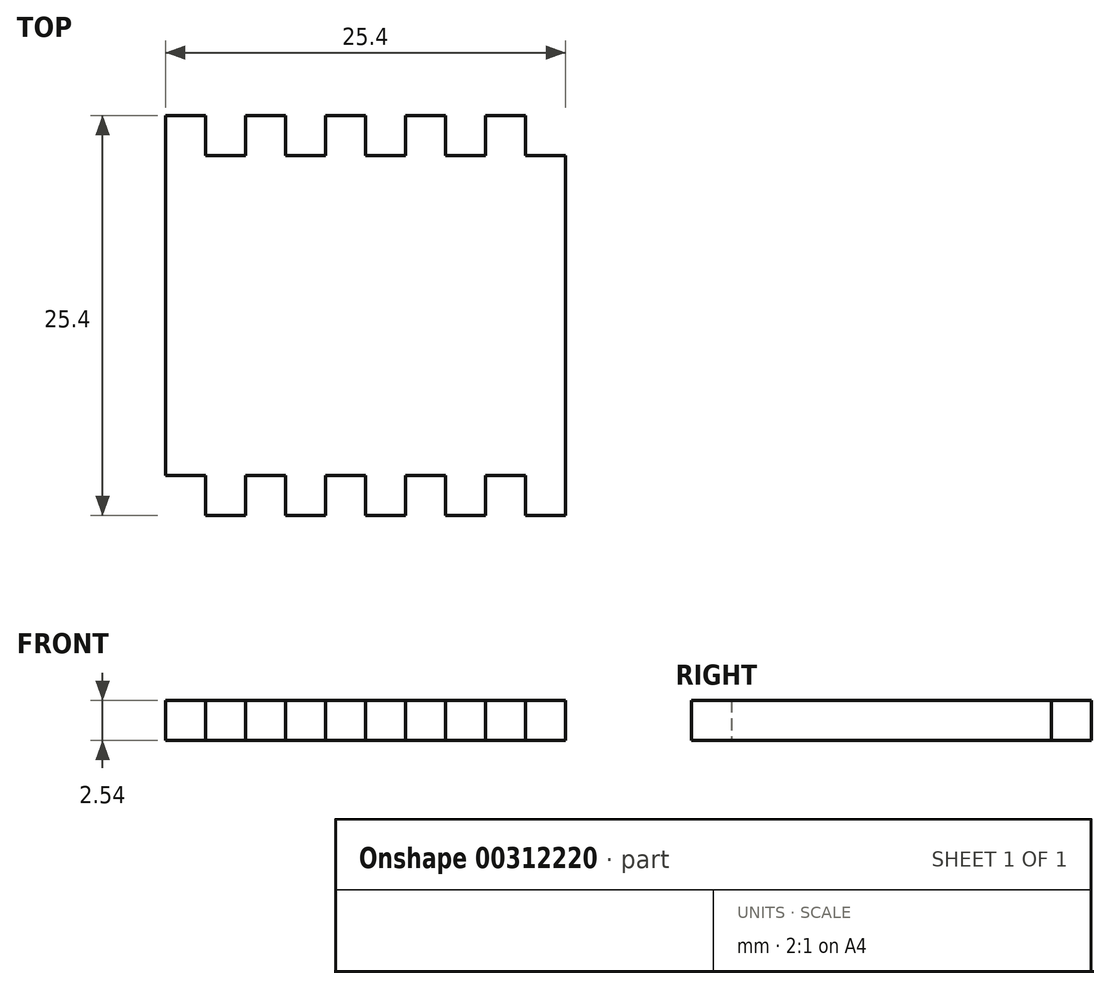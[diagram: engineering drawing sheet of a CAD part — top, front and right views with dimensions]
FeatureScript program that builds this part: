
annotation { "Feature Type Name" : "Feature", "Feature Type Description" : "" }
export const myFeature = defineFeature(function(context is Context, id is Id, definition is map)
    precondition{}
    {
        {
            var Q0;
            Q0=qCreatedBy(makeId("Top.planeOp"),FACE);
            var sketch = newSketch(context, id + "F0", { "sketchPlane" : qUnion([Q0])});
            skLineSegment(sketch, "E0.left", {"start": v(12.7, 10.16) * mm, "end": v(12.7, -12.7) * mm});
            skLineSegment(sketch, "E0.right", {"start": v(-12.7, 12.7) * mm, "end": v(-12.7, -10.16) * mm});
            skPoint(sketch, "E0.middle", {"position": v(0, 0) * mm});
            skLineSegment(sketch, "E1", {"start": v(-12.7, 12.7) * mm, "end": v(-10.16, 12.7) * mm});
            skLineSegment(sketch, "E2", {"start": v(-10.16, 12.7) * mm, "end": v(-10.16, 10.16) * mm});
            skLineSegment(sketch, "E3", {"start": v(-10.16, 10.16) * mm, "end": v(-7.62, 10.16) * mm});
            skLineSegment(sketch, "E4", {"start": v(-7.62, 10.16) * mm, "end": v(-7.62, 12.7) * mm});
            skLineSegment(sketch, "E5", {"start": v(-7.62, 12.7) * mm, "end": v(-5.08, 12.7) * mm});
            skLineSegment(sketch, "E6", {"start": v(-5.08, 12.7) * mm, "end": v(-5.08, 10.16) * mm});
            skLineSegment(sketch, "E7", {"start": v(-5.08, 10.16) * mm, "end": v(-2.54, 10.16) * mm});
            skLineSegment(sketch, "E8", {"start": v(-2.54, 10.16) * mm, "end": v(-2.54, 12.7) * mm});
            skLineSegment(sketch, "E9", {"start": v(-2.54, 12.7) * mm, "end": v(0, 12.7) * mm});
            skLineSegment(sketch, "E10", {"start": v(0, 12.7) * mm, "end": v(0, 10.16) * mm});
            skLineSegment(sketch, "E11", {"start": v(0, 10.16) * mm, "end": v(2.54, 10.16) * mm});
            skLineSegment(sketch, "E12", {"start": v(2.54, 10.16) * mm, "end": v(2.54, 12.7) * mm});
            skLineSegment(sketch, "E13", {"start": v(2.54, 12.7) * mm, "end": v(5.08, 12.7) * mm});
            skLineSegment(sketch, "E14", {"start": v(5.08, 12.7) * mm, "end": v(5.08, 10.16) * mm});
            skLineSegment(sketch, "E15", {"start": v(5.08, 10.16) * mm, "end": v(7.62, 10.16) * mm});
            skLineSegment(sketch, "E16", {"start": v(7.62, 10.16) * mm, "end": v(7.62, 12.7) * mm});
            skLineSegment(sketch, "E17", {"start": v(7.62, 12.7) * mm, "end": v(10.16, 12.7) * mm});
            skLineSegment(sketch, "E18", {"start": v(10.16, 12.7) * mm, "end": v(10.16, 10.16) * mm});
            skLineSegment(sketch, "E19", {"start": v(10.16, 10.16) * mm, "end": v(12.7, 10.16) * mm});
            skLineSegment(sketch, "E20", {"start": v(12.7, -12.7) * mm, "end": v(10.16, -12.7) * mm});
            skLineSegment(sketch, "E21", {"start": v(10.16, -12.7) * mm, "end": v(10.16, -10.16) * mm});
            skLineSegment(sketch, "E22", {"start": v(10.16, -10.16) * mm, "end": v(7.62, -10.16) * mm});
            skLineSegment(sketch, "E23", {"start": v(7.62, -10.16) * mm, "end": v(7.62, -12.7) * mm});
            skLineSegment(sketch, "E24", {"start": v(7.62, -12.7) * mm, "end": v(5.08, -12.7) * mm});
            skLineSegment(sketch, "E25", {"start": v(5.08, -12.7) * mm, "end": v(5.08, -10.16) * mm});
            skLineSegment(sketch, "E26", {"start": v(5.08, -10.16) * mm, "end": v(2.54, -10.16) * mm});
            skLineSegment(sketch, "E27", {"start": v(2.54, -10.16) * mm, "end": v(2.54, -12.7) * mm});
            skLineSegment(sketch, "E28", {"start": v(2.54, -12.7) * mm, "end": v(0, -12.7) * mm});
            skLineSegment(sketch, "E29", {"start": v(0, -12.7) * mm, "end": v(0, -10.16) * mm});
            skLineSegment(sketch, "E30", {"start": v(0, -10.16) * mm, "end": v(-2.54, -10.16) * mm});
            skLineSegment(sketch, "E31", {"start": v(-2.54, -10.16) * mm, "end": v(-2.54, -12.7) * mm});
            skLineSegment(sketch, "E32", {"start": v(-2.54, -12.7) * mm, "end": v(-5.08, -12.7) * mm});
            skLineSegment(sketch, "E33", {"start": v(-5.08, -12.7) * mm, "end": v(-5.08, -10.16) * mm});
            skLineSegment(sketch, "E34", {"start": v(-5.08, -10.16) * mm, "end": v(-7.62, -10.16) * mm});
            skLineSegment(sketch, "E35", {"start": v(-7.62, -10.16) * mm, "end": v(-7.62, -12.7) * mm});
            skLineSegment(sketch, "E36", {"start": v(-7.62, -12.7) * mm, "end": v(-10.16, -12.7) * mm});
            skLineSegment(sketch, "E37", {"start": v(-10.16, -12.7) * mm, "end": v(-10.16, -10.16) * mm});
            skLineSegment(sketch, "E38", {"start": v(-10.16, -10.16) * mm, "end": v(-12.7, -10.16) * mm});
            skSolve(sketch);
        }
        {
            var Q0;
            Q0=makeQuery(id+"F0.imprint","IMPRINT",FACE,{"disambiguationData":[TD([[makeQuery(id+"F0.imprint","IMPRINT",EDGE,{"derivedFrom":sQuery(id+"F0.wireOp",EDGE,"E0.left")}),-1.0]])]});
            extrude(context, id + "F1", {"entities" : qUnion([Q0]), "depth" : 2.54 * mm});
        }
    });
